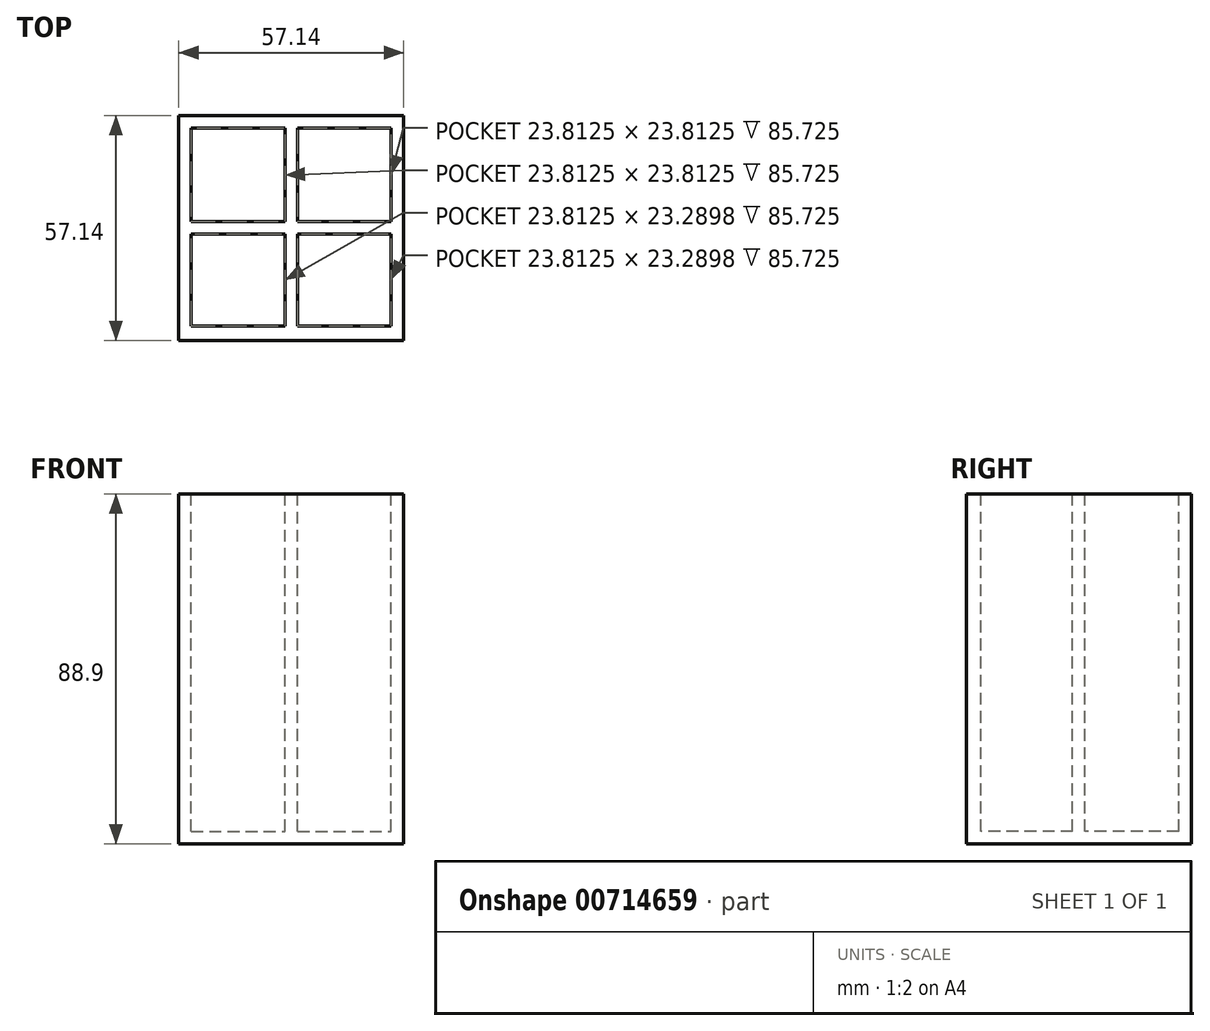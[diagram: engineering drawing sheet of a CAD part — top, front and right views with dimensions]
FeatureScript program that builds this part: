
annotation { "Feature Type Name" : "Feature", "Feature Type Description" : "" }
export const myFeature = defineFeature(function(context is Context, id is Id, definition is map)
    precondition{}
    {
        {
            var Q0;
            Q0=qCreatedBy(makeId("Top.planeOp"),FACE);
            var sketch = newSketch(context, id + "F0", { "sketchPlane" : qUnion([Q0])});
            skLineSegment(sketch, "E0.bottom", {"start": v(-28.58, 28.58) * mm, "end": v(28.58, 28.58) * mm});
            skLineSegment(sketch, "E0.top", {"start": v(-28.58, -28.58) * mm, "end": v(28.57, -28.58) * mm});
            skLineSegment(sketch, "E0.left", {"start": v(-28.57, 28.58) * mm, "end": v(-28.58, -28.58) * mm});
            skLineSegment(sketch, "E0.right", {"start": v(28.58, 28.58) * mm, "end": v(28.57, -28.58) * mm});
            skPoint(sketch, "E0.middle", {"position": v(0, 0) * mm});
            skSolve(sketch);
        }
        {
            var Q0;
            Q0 = qSketchRegion(id + "F0", true);
            extrude(context, id + "F1", {"entities" : qUnion([Q0]), "depth" : 88.9 * mm, "offsetDistance" : 25.4 * mm});
        }
        {
            var Q0;
            Q0=makeQuery(id+"F1.opExtrude","CAP_FACE",FACE,{"disambiguationData":[OSD([sQuery(id+"F0.wireOp",EDGE,"E0.bottom"),sQuery(id+"F0.wireOp",EDGE,"E0.top"),sQuery(id+"F0.wireOp",EDGE,"E0.left"),sQuery(id+"F0.wireOp",EDGE,"E0.right")])],"isStart":false});
            var sketch = newSketch(context, id + "F2", { "sketchPlane" : qUnion([Q0])});
            skLineSegment(sketch, "E1", {"start": v(1.59, 25.4) * mm, "end": v(1.59, 1.59) * mm});
            skLineSegment(sketch, "E2", {"start": v(-1.59, 25.4) * mm, "end": v(-1.59, 1.59) * mm});
            skLineSegment(sketch, "E3", {"start": v(-25.4, -1.59) * mm, "end": v(-1.59, -1.59) * mm});
            skLineSegment(sketch, "E4", {"start": v(-25.4, 1.59) * mm, "end": v(-1.59, 1.59) * mm});
            skLineSegment(sketch, "E5", {"start": v(-25.4, 25.4) * mm, "end": v(-25.4, 1.59) * mm});
            skLineSegment(sketch, "E6", {"start": v(-25.4, -24.88) * mm, "end": v(-1.59, -24.88) * mm});
            skLineSegment(sketch, "E7.trimOffspring", {"start": v(1.59, -1.59) * mm, "end": v(1.59, -24.88) * mm});
            skLineSegment(sketch, "E8.trimOffspring", {"start": v(1.59, 1.59) * mm, "end": v(25.4, 1.59) * mm});
            skLineSegment(sketch, "E9.trimOffspring", {"start": v(-1.59, -1.59) * mm, "end": v(-1.59, -24.88) * mm});
            skLineSegment(sketch, "E10.trimOffspring", {"start": v(1.59, -1.59) * mm, "end": v(25.4, -1.59) * mm});
            skLineSegment(sketch, "E11", {"start": v(-25.4, 25.4) * mm, "end": v(-1.59, 25.4) * mm});
            skLineSegment(sketch, "E12", {"start": v(25.4, 25.4) * mm, "end": v(25.4, 1.59) * mm});
            skLineSegment(sketch, "E13.trimOffspring", {"start": v(25.4, -1.59) * mm, "end": v(25.4, -24.88) * mm});
            skLineSegment(sketch, "E14.trimOffspring", {"start": v(1.59, -24.88) * mm, "end": v(25.4, -24.88) * mm});
            skLineSegment(sketch, "E15.trimOffspring", {"start": v(-25.4, -1.59) * mm, "end": v(-25.4, -24.88) * mm});
            skLineSegment(sketch, "E16.trimOffspring", {"start": v(1.59, 25.4) * mm, "end": v(25.4, 25.4) * mm});
            skSolve(sketch);
        }
        {
            var Q0;
            Q0 = qSketchRegion(id + "F2", true);
            extrude(context, id + "F3", {"entities" : qUnion([Q0]), "operationType" : NewBodyOperationType.REMOVE, "oppositeDirection" : true, "depth" : 85.72 * mm, "offsetDistance" : 25.4 * mm});
        }
    });
